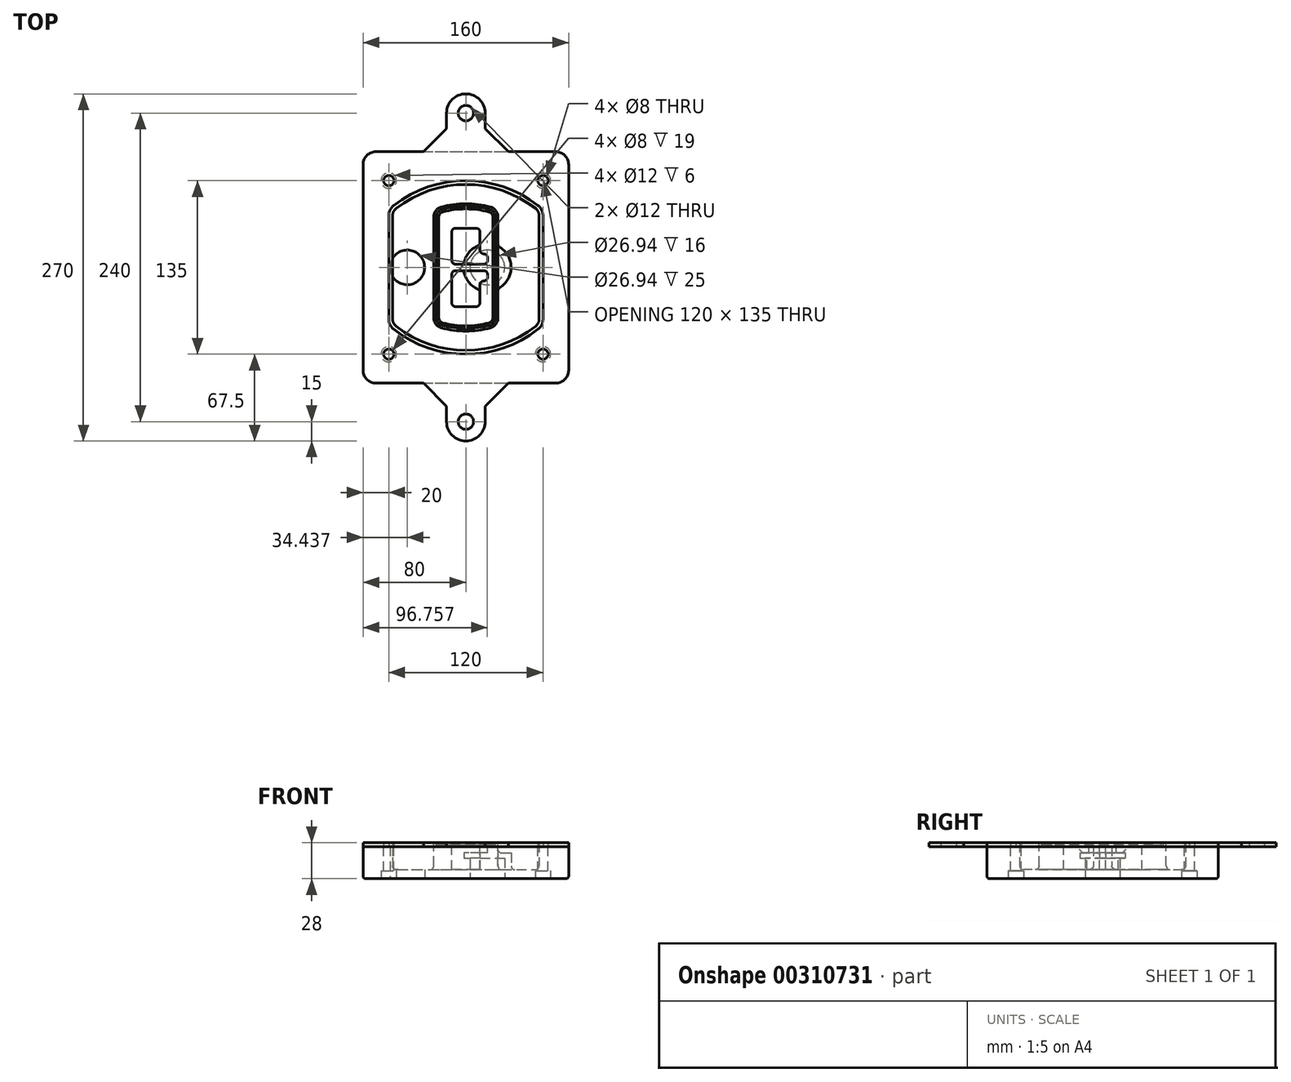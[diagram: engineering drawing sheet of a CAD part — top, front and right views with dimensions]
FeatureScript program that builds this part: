
annotation { "Feature Type Name" : "Feature", "Feature Type Description" : "" }
export const myFeature = defineFeature(function(context is Context, id is Id, definition is map)
    precondition{}
    {
        {
            var Q0;
            Q0=qCreatedBy(makeId("Top.planeOp"),FACE);
            var sketch = newSketch(context, id + "F0", { "sketchPlane" : qUnion([Q0])});
            skPoint(sketch, "E0.rect.middle", {"position": v(0, 0) * mm});
            skLineSegment(sketch, "E1.bottom", {"start": v(-70, -90) * mm, "end": v(70, -90) * mm});
            skLineSegment(sketch, "E1.top", {"start": v(-70, 90) * mm, "end": v(70, 90) * mm});
            skLineSegment(sketch, "E1.left", {"start": v(-80, -80) * mm, "end": v(-80, 80) * mm});
            skLineSegment(sketch, "E1.right", {"start": v(80, -80) * mm, "end": v(80, 80) * mm});
            skLineSegment(sketch, "E2", {"start": v(-80, 90) * mm, "end": v(80, -90) * mm, "construction": true});
            skLineSegment(sketch, "E3", {"start": v(80, 90) * mm, "end": v(-80, -90) * mm, "construction": true});
            skCircle(sketch, "E4", {"center": v(-60, 67.5) * mm, "radius": 4 * mm});
            skCircle(sketch, "E5", {"center": v(60, 67.5) * mm, "radius": 4 * mm});
            skCircle(sketch, "E6", {"center": v(60, -67.5) * mm, "radius": 4 * mm});
            skCircle(sketch, "E7", {"center": v(-60, -67.5) * mm, "radius": 4 * mm});
            skLineSegment(sketch, "E8", {"start": v(-60, 67.5) * mm, "end": v(60, 67.5) * mm, "construction": true});
            skLineSegment(sketch, "E9", {"start": v(60, 67.5) * mm, "end": v(60, -67.5) * mm, "construction": true});
            skLineSegment(sketch, "E10", {"start": v(60, -67.5) * mm, "end": v(-60, -67.5) * mm, "construction": true});
            skLineSegment(sketch, "E11", {"start": v(-60, -67.5) * mm, "end": v(-60, 67.5) * mm, "construction": true});
            skLineSegment(sketch, "E12", {"start": v(-60, 40.3) * mm, "end": v(-60, -40.3) * mm});
            skLineSegment(sketch, "E13", {"start": v(60, 40.3) * mm, "end": v(60, -40.3) * mm});
            skArc(sketch, "E14", {"start": v(56.15, 48.18) * mm, "mid": v(0, 67.5) * mm, "end": v(-56.15, 48.18) * mm});
            skArc(sketch, "E15", {"start": v(-56.15, -48.18) * mm, "mid": v(0, -67.5) * mm, "end": v(56.15, -48.18) * mm});
            skLineSegment(sketch, "E16", {"start": v(-60, 0) * mm, "end": v(60, 0) * mm, "construction": true});
            skPoint(sketch, "E17.visualSharp", {"position": v(-60, -45) * mm});
            skArc(sketch, "E17.filletArc", {"start": v(-60, -40.3) * mm, "mid": v(-58.99, -44.68) * mm, "end": v(-56.15, -48.18) * mm});
            skPoint(sketch, "E18.visualSharp", {"position": v(-60, 45) * mm});
            skArc(sketch, "E18.filletArc", {"start": v(-56.15, 48.18) * mm, "mid": v(-58.99, 44.68) * mm, "end": v(-60, 40.3) * mm});
            skPoint(sketch, "E19.visualSharp", {"position": v(60, 45) * mm});
            skArc(sketch, "E19.filletArc", {"start": v(60, 40.3) * mm, "mid": v(58.99, 44.68) * mm, "end": v(56.15, 48.18) * mm});
            skPoint(sketch, "E20.visualSharp", {"position": v(60, -45) * mm});
            skArc(sketch, "E20.filletArc", {"start": v(56.15, -48.18) * mm, "mid": v(58.99, -44.68) * mm, "end": v(60, -40.3) * mm});
            skPoint(sketch, "E21.visualSharp", {"position": v(-80, 90) * mm});
            skArc(sketch, "E21.filletArc", {"start": v(-70, 90) * mm, "mid": v(-77.07, 87.07) * mm, "end": v(-80, 80) * mm});
            skPoint(sketch, "E22.visualSharp", {"position": v(80, 90) * mm});
            skArc(sketch, "E22.filletArc", {"start": v(80, 80) * mm, "mid": v(77.07, 87.07) * mm, "end": v(70, 90) * mm});
            skPoint(sketch, "E23.visualSharp", {"position": v(80, -90) * mm});
            skArc(sketch, "E23.filletArc", {"start": v(70, -90) * mm, "mid": v(77.07, -87.07) * mm, "end": v(80, -80) * mm});
            skPoint(sketch, "E24.visualSharp", {"position": v(-80, -90) * mm});
            skArc(sketch, "E24.filletArc", {"start": v(-80, -80) * mm, "mid": v(-77.07, -87.07) * mm, "end": v(-70, -90) * mm});
            skArc(sketch, "E25.0", {"start": v(57, 40.3) * mm, "mid": v(56.3, 43.36) * mm, "end": v(54.3, 45.81) * mm});
            skLineSegment(sketch, "E25.1", {"start": v(57, 40.3) * mm, "end": v(57, -40.3) * mm});
            skArc(sketch, "E25.2", {"start": v(54.3, -45.81) * mm, "mid": v(56.3, -43.36) * mm, "end": v(57, -40.3) * mm});
            skArc(sketch, "E25.3", {"start": v(-54.3, -45.81) * mm, "mid": v(0, -64.5) * mm, "end": v(54.3, -45.81) * mm});
            skArc(sketch, "E25.4", {"start": v(-57, -40.3) * mm, "mid": v(-56.3, -43.36) * mm, "end": v(-54.3, -45.81) * mm});
            skArc(sketch, "E25.5", {"start": v(54.3, 45.81) * mm, "mid": v(0, 64.5) * mm, "end": v(-54.3, 45.81) * mm});
            skLineSegment(sketch, "E25.6", {"start": v(-57, 40.3) * mm, "end": v(-57, -40.3) * mm});
            skArc(sketch, "E25.7", {"start": v(-54.3, 45.81) * mm, "mid": v(-56.3, 43.36) * mm, "end": v(-57, 40.3) * mm});
            skArc(sketch, "E26.0", {"start": v(-58.62, 51.33) * mm, "mid": v(-62.58, 46.43) * mm, "end": v(-64, 40.3) * mm});
            skArc(sketch, "E26.1", {"start": v(58.62, 51.33) * mm, "mid": v(0, 71.5) * mm, "end": v(-58.62, 51.33) * mm});
            skArc(sketch, "E26.2", {"start": v(64, 40.3) * mm, "mid": v(62.58, 46.43) * mm, "end": v(58.62, 51.33) * mm});
            skLineSegment(sketch, "E26.3", {"start": v(64, 40.3) * mm, "end": v(64, -40.3) * mm});
            skArc(sketch, "E26.4", {"start": v(58.62, -51.33) * mm, "mid": v(62.58, -46.43) * mm, "end": v(64, -40.3) * mm});
            skLineSegment(sketch, "E26.5", {"start": v(-64, 40.3) * mm, "end": v(-64, -40.3) * mm});
            skArc(sketch, "E26.6", {"start": v(-58.62, -51.33) * mm, "mid": v(0, -71.5) * mm, "end": v(58.62, -51.33) * mm});
            skArc(sketch, "E26.7", {"start": v(-64, -40.3) * mm, "mid": v(-62.58, -46.43) * mm, "end": v(-58.62, -51.33) * mm});
            skSolve(sketch);
        }
        {
            var Q0;
            Q0=makeQuery(id+"F0.imprint","IMPRINT",FACE,{"disambiguationData":[TD([[makeQuery(id+"F0.imprint","IMPRINT",EDGE,{"derivedFrom":sQuery(id+"F0.wireOp",EDGE,"E1.bottom")}),1.0]])]});
            var Q1;
            Q1=makeQuery(id+"F0.imprint","IMPRINT",FACE,{"disambiguationData":[TD([[makeQuery(id+"F0.imprint","IMPRINT",EDGE,{"derivedFrom":sQuery(id+"F0.wireOp",EDGE,"E12")}),1.0]])]});
            var Q2;
            Q2=makeQuery(id+"F0.imprint","IMPRINT",FACE,{"disambiguationData":[TD([[makeQuery(id+"F0.imprint","IMPRINT",EDGE,{"derivedFrom":sQuery(id+"F0.wireOp",EDGE,"E25.0")}),1.0]])]});
            var Q3;
            Q3=makeQuery(id+"F0.imprint","IMPRINT",FACE,{"disambiguationData":[TD([[makeQuery(id+"F0.imprint","IMPRINT",EDGE,{"derivedFrom":sQuery(id+"F0.wireOp",EDGE,"E12")}),-1.0]])]});
            extrude(context, id + "F1", {"entities" : qUnion([Q0, Q1, Q2, Q3]), "oppositeDirection" : true, "depth" : 25 * mm});
        }
        {
            var Q0;
            Q0=makeQuery(id+"F0.imprint","IMPRINT",FACE,{"disambiguationData":[TD([[makeQuery(id+"F0.imprint","IMPRINT",EDGE,{"derivedFrom":sQuery(id+"F0.wireOp",EDGE,"E12")}),1.0]])]});
            extrude(context, id + "F2", {"entities" : qUnion([Q0]), "operationType" : NewBodyOperationType.ADD, "depth" : 3 * mm});
        }
        {
            var Q0;
            Q0=makeQuery(id+"F0.imprint","IMPRINT",FACE,{"disambiguationData":[TD([[makeQuery(id+"F0.imprint","IMPRINT",EDGE,{"derivedFrom":sQuery(id+"F0.wireOp",EDGE,"E25.0")}),1.0]])]});
            extrude(context, id + "F3", {"entities" : qUnion([Q0]), "operationType" : NewBodyOperationType.REMOVE, "oppositeDirection" : true, "depth" : 18 * mm});
        }
        {
            var Q0;
            Q0=makeQuery(id+"F2.opExtrude","CAP_FACE",FACE,{"disambiguationData":[OSD([sQuery(id+"F0.wireOp",EDGE,"E12"),sQuery(id+"F0.wireOp",EDGE,"E13"),sQuery(id+"F0.wireOp",EDGE,"E14"),sQuery(id+"F0.wireOp",EDGE,"E15"),sQuery(id+"F0.wireOp",EDGE,"E17.filletArc"),sQuery(id+"F0.wireOp",EDGE,"E18.filletArc"),sQuery(id+"F0.wireOp",EDGE,"E19.filletArc"),sQuery(id+"F0.wireOp",EDGE,"E20.filletArc"),sQuery(id+"F0.wireOp",EDGE,"E25.0"),sQuery(id+"F0.wireOp",EDGE,"E25.1"),sQuery(id+"F0.wireOp",EDGE,"E25.2"),sQuery(id+"F0.wireOp",EDGE,"E25.3"),sQuery(id+"F0.wireOp",EDGE,"E25.4"),sQuery(id+"F0.wireOp",EDGE,"E25.5"),sQuery(id+"F0.wireOp",EDGE,"E25.6"),sQuery(id+"F0.wireOp",EDGE,"E25.7")])],"isStart":false});
            var sketch = newSketch(context, id + "F4", { "sketchPlane" : qUnion([Q0])});
            skArc(sketch, "E27.0", {"start": v(-19.08, -46.97) * mm, "mid": v(0, -49.5) * mm, "end": v(19.08, -46.97) * mm});
            skArc(sketch, "E28.0", {"start": v(19.08, 46.97) * mm, "mid": v(0, 49.5) * mm, "end": v(-19.08, 46.97) * mm});
            skLineSegment(sketch, "E29", {"start": v(-25, 39.25) * mm, "end": v(-25, -39.25) * mm});
            skLineSegment(sketch, "E30", {"start": v(25, 39.25) * mm, "end": v(25, -39.25) * mm});
            skLineSegment(sketch, "E31", {"start": v(-25, 45.1) * mm, "end": v(25, 45.1) * mm, "construction": true});
            skLineSegment(sketch, "E32", {"start": v(-25, -45.1) * mm, "end": v(25, -45.1) * mm, "construction": true});
            skPoint(sketch, "E33.visualSharp", {"position": v(-25, 45.1) * mm});
            skArc(sketch, "E33.filletArc", {"start": v(-19.08, 46.97) * mm, "mid": v(-23.35, 44.11) * mm, "end": v(-25, 39.25) * mm});
            skPoint(sketch, "E34.visualSharp", {"position": v(25, 45.1) * mm});
            skArc(sketch, "E34.filletArc", {"start": v(25, 39.25) * mm, "mid": v(23.35, 44.11) * mm, "end": v(19.08, 46.97) * mm});
            skPoint(sketch, "E35.visualSharp", {"position": v(25, -45.1) * mm});
            skArc(sketch, "E35.filletArc", {"start": v(19.08, -46.97) * mm, "mid": v(23.35, -44.11) * mm, "end": v(25, -39.25) * mm});
            skPoint(sketch, "E36.visualSharp", {"position": v(-25, -45.1) * mm});
            skArc(sketch, "E36.filletArc", {"start": v(-25, -39.25) * mm, "mid": v(-23.35, -44.11) * mm, "end": v(-19.08, -46.97) * mm});
            skArc(sketch, "E37.0", {"start": v(54.3, 45.81) * mm, "mid": v(0, 64.5) * mm, "end": v(-54.3, 45.81) * mm});
            skArc(sketch, "E37.1", {"start": v(-54.3, 45.81) * mm, "mid": v(-56.3, 43.36) * mm, "end": v(-57, 40.3) * mm});
            skLineSegment(sketch, "E37.2", {"start": v(-57, 40.3) * mm, "end": v(-57, -40.3) * mm});
            skArc(sketch, "E37.3", {"start": v(-57, -40.3) * mm, "mid": v(-56.3, -43.36) * mm, "end": v(-54.3, -45.81) * mm});
            skArc(sketch, "E37.4", {"start": v(-54.3, -45.81) * mm, "mid": v(0, -64.5) * mm, "end": v(54.3, -45.81) * mm});
            skArc(sketch, "E37.5", {"start": v(54.3, -45.81) * mm, "mid": v(56.3, -43.36) * mm, "end": v(57, -40.3) * mm});
            skLineSegment(sketch, "E37.6", {"start": v(57, 40.3) * mm, "end": v(57, -40.3) * mm});
            skArc(sketch, "E37.7", {"start": v(57, 40.3) * mm, "mid": v(56.3, 43.36) * mm, "end": v(54.3, 45.81) * mm});
            skLineSegment(sketch, "E38.0", {"start": v(23, 39.25) * mm, "end": v(23, -39.25) * mm});
            skArc(sketch, "E38.1", {"start": v(18.56, -45.04) * mm, "mid": v(21.76, -42.9) * mm, "end": v(23, -39.25) * mm});
            skArc(sketch, "E38.2", {"start": v(-18.56, -45.04) * mm, "mid": v(0, -47.5) * mm, "end": v(18.56, -45.04) * mm});
            skArc(sketch, "E38.3", {"start": v(-23, -39.25) * mm, "mid": v(-21.76, -42.9) * mm, "end": v(-18.56, -45.04) * mm});
            skLineSegment(sketch, "E38.4", {"start": v(-23, 39.25) * mm, "end": v(-23, -39.25) * mm});
            skArc(sketch, "E38.5", {"start": v(23, 39.25) * mm, "mid": v(21.76, 42.9) * mm, "end": v(18.56, 45.04) * mm});
            skArc(sketch, "E38.6", {"start": v(-18.56, 45.04) * mm, "mid": v(-21.76, 42.9) * mm, "end": v(-23, 39.25) * mm});
            skArc(sketch, "E38.7", {"start": v(18.56, 45.04) * mm, "mid": v(0, 47.5) * mm, "end": v(-18.56, 45.04) * mm});
            skArc(sketch, "E39.0", {"start": v(21, 39.25) * mm, "mid": v(20.18, 41.68) * mm, "end": v(18.04, 43.1) * mm});
            skLineSegment(sketch, "E39.1", {"start": v(21, 39.25) * mm, "end": v(21, -39.25) * mm});
            skArc(sketch, "E39.2", {"start": v(18.04, -43.1) * mm, "mid": v(20.18, -41.68) * mm, "end": v(21, -39.25) * mm});
            skArc(sketch, "E39.3", {"start": v(-18.04, -43.1) * mm, "mid": v(0, -45.5) * mm, "end": v(18.04, -43.1) * mm});
            skArc(sketch, "E39.4", {"start": v(-21, -39.25) * mm, "mid": v(-20.18, -41.68) * mm, "end": v(-18.04, -43.1) * mm});
            skArc(sketch, "E39.5", {"start": v(18.04, 43.1) * mm, "mid": v(0, 45.5) * mm, "end": v(-18.04, 43.1) * mm});
            skLineSegment(sketch, "E39.6", {"start": v(-21, 39.25) * mm, "end": v(-21, -39.25) * mm});
            skArc(sketch, "E39.7", {"start": v(-18.04, 43.1) * mm, "mid": v(-20.18, 41.68) * mm, "end": v(-21, 39.25) * mm});
            skLineSegment(sketch, "E40", {"start": v(-25, 0) * mm, "end": v(25, 0) * mm, "construction": true});
            skLineSegment(sketch, "E41", {"start": v(-11, 5.5) * mm, "end": v(-11, 27.5) * mm});
            skLineSegment(sketch, "E42", {"start": v(-8, 30.5) * mm, "end": v(8, 30.5) * mm});
            skLineSegment(sketch, "E43", {"start": v(11, 27.5) * mm, "end": v(11, 13.5) * mm});
            skLineSegment(sketch, "E44", {"start": v(14, 10.5) * mm, "end": v(14, 10.5) * mm});
            skLineSegment(sketch, "E45", {"start": v(17, 7.5) * mm, "end": v(17, 5.5) * mm});
            skLineSegment(sketch, "E46", {"start": v(14, 2.5) * mm, "end": v(-8, 2.5) * mm});
            skPoint(sketch, "E47.visualSharp", {"position": v(-11, 30.5) * mm});
            skArc(sketch, "E47.filletArc", {"start": v(-8, 30.5) * mm, "mid": v(-10.12, 29.62) * mm, "end": v(-11, 27.5) * mm});
            skPoint(sketch, "E48.visualSharp", {"position": v(11, 30.5) * mm});
            skArc(sketch, "E48.filletArc", {"start": v(11, 27.5) * mm, "mid": v(10.12, 29.62) * mm, "end": v(8, 30.5) * mm});
            skPoint(sketch, "E49.visualSharp", {"position": v(11, 10.5) * mm});
            skArc(sketch, "E49.filletArc", {"start": v(11, 13.5) * mm, "mid": v(11.88, 11.38) * mm, "end": v(14, 10.5) * mm});
            skPoint(sketch, "E50.visualSharp", {"position": v(17, 10.5) * mm});
            skArc(sketch, "E50.filletArc", {"start": v(17, 7.5) * mm, "mid": v(16.12, 9.62) * mm, "end": v(14, 10.5) * mm});
            skPoint(sketch, "E51.visualSharp", {"position": v(17, 2.5) * mm});
            skArc(sketch, "E51.filletArc", {"start": v(14, 2.5) * mm, "mid": v(16.12, 3.38) * mm, "end": v(17, 5.5) * mm});
            skPoint(sketch, "E52.visualSharp", {"position": v(-11, 2.5) * mm});
            skArc(sketch, "E52.filletArc", {"start": v(-11, 5.5) * mm, "mid": v(-10.12, 3.38) * mm, "end": v(-8, 2.5) * mm});
            skLineSegment(sketch, "E53.0.MirrorCS", {"start": v(14, -2.5) * mm, "end": v(-8, -2.5) * mm});
            skArc(sketch, "E54.0.MirrorCS", {"start": v(-11, -5.5) * mm, "mid": v(-10.12, -3.38) * mm, "end": v(-8, -2.5) * mm});
            skLineSegment(sketch, "E55.0.MirrorCS", {"start": v(-11, -5.5) * mm, "end": v(-11, -27.5) * mm});
            skArc(sketch, "E56.0.MirrorCS", {"start": v(-8, -30.5) * mm, "mid": v(-10.12, -29.62) * mm, "end": v(-11, -27.5) * mm});
            skLineSegment(sketch, "E57.0.MirrorCS", {"start": v(-8, -30.5) * mm, "end": v(8, -30.5) * mm});
            skArc(sketch, "E58.0.MirrorCS", {"start": v(11, -27.5) * mm, "mid": v(10.12, -29.62) * mm, "end": v(8, -30.5) * mm});
            skLineSegment(sketch, "E59.0.MirrorCS", {"start": v(11, -27.5) * mm, "end": v(11, -13.5) * mm});
            skArc(sketch, "E60.0.MirrorCS", {"start": v(11, -13.5) * mm, "mid": v(11.88, -11.38) * mm, "end": v(14, -10.5) * mm});
            skArc(sketch, "E61.0.MirrorCS", {"start": v(17, -7.5) * mm, "mid": v(16.12, -9.62) * mm, "end": v(14, -10.5) * mm});
            skLineSegment(sketch, "E62.0.MirrorCS", {"start": v(17, -7.5) * mm, "end": v(17, -5.5) * mm});
            skArc(sketch, "E63.0.MirrorCS", {"start": v(14, -2.5) * mm, "mid": v(16.12, -3.38) * mm, "end": v(17, -5.5) * mm});
            skSolve(sketch);
        }
        {
            var Q0;
            Q0=makeQuery(id+"F4.imprint","IMPRINT",FACE,{"disambiguationData":[TD([[makeQuery(id+"F4.imprint","IMPRINT",EDGE,{"derivedFrom":sQuery(id+"F4.wireOp",EDGE,"E27.0")}),1.0]])]});
            var Q1;
            Q1=makeQuery(id+"F4.imprint","IMPRINT",FACE,{"disambiguationData":[TD([[makeQuery(id+"F4.imprint","IMPRINT",EDGE,{"derivedFrom":sQuery(id+"F4.wireOp",EDGE,"E38.0")}),-1.0]])]});
            var Q2;
            Q2=makeQuery(id+"F4.imprint","IMPRINT",FACE,{"disambiguationData":[TD([[makeQuery(id+"F4.imprint","IMPRINT",EDGE,{"derivedFrom":sQuery(id+"F4.wireOp",EDGE,"E39.0")}),1.0]])]});
            extrude(context, id + "F5", {"entities" : qUnion([Q0, Q1, Q2]), "operationType" : NewBodyOperationType.ADD, "endBound" : BoundingType.UP_TO_NEXT, "oppositeDirection" : true, "depth" : 25 * mm});
        }
        {
            var Q0;
            Q0=makeQuery(id+"F4.imprint","IMPRINT",FACE,{"disambiguationData":[TD([[makeQuery(id+"F4.imprint","IMPRINT",EDGE,{"derivedFrom":sQuery(id+"F4.wireOp",EDGE,"E38.0")}),-1.0]])]});
            extrude(context, id + "F6", {"entities" : qUnion([Q0]), "operationType" : NewBodyOperationType.REMOVE, "oppositeDirection" : true, "depth" : 2 * mm});
        }
        {
            var Q0;
            Q0=makeQuery(id+"F1.opExtrude","CAP_FACE",FACE,{"disambiguationData":[OSD([sQuery(id+"F0.wireOp",EDGE,"E1.bottom"),sQuery(id+"F0.wireOp",EDGE,"E1.top"),sQuery(id+"F0.wireOp",EDGE,"E1.left"),sQuery(id+"F0.wireOp",EDGE,"E1.right"),sQuery(id+"F0.wireOp",EDGE,"E4"),sQuery(id+"F0.wireOp",EDGE,"E5"),sQuery(id+"F0.wireOp",EDGE,"E6"),sQuery(id+"F0.wireOp",EDGE,"E7"),sQuery(id+"F0.wireOp",EDGE,"E21.filletArc"),sQuery(id+"F0.wireOp",EDGE,"E22.filletArc"),sQuery(id+"F0.wireOp",EDGE,"E23.filletArc"),sQuery(id+"F0.wireOp",EDGE,"E24.filletArc")])],"isStart":false});
            var sketch = newSketch(context, id + "F7", { "sketchPlane" : qUnion([Q0])});
            skCircle(sketch, "E64", {"center": v(16.76, 0) * mm, "radius": 13.47 * mm});
            skCircle(sketch, "E65", {"center": v(-45.56, 0) * mm, "radius": 13.47 * mm});
            skLineSegment(sketch, "E66", {"start": v(80, 0) * mm, "end": v(-80, 0) * mm});
            skCircle(sketch, "E67", {"center": v(16.76, 0) * mm, "radius": 18.47 * mm});
            skCircle(sketch, "E68", {"center": v(60, -67.5) * mm, "radius": 6 * mm});
            skCircle(sketch, "E69", {"center": v(-60, -67.5) * mm, "radius": 6 * mm});
            skCircle(sketch, "E70", {"center": v(-60, 67.5) * mm, "radius": 6 * mm});
            skCircle(sketch, "E71", {"center": v(60, 67.5) * mm, "radius": 6 * mm});
            skSolve(sketch);
        }
        {
            var Q0;
            {var subQ1=sQuery(id+"F7.wireOp",EDGE,"E66");var subQ4=sQuery(id+"F7.wireOp",EDGE,"E64");var subQ6=makeQuery(id+"F7.imprint","INTERSECT",VERTEX,{"disambiguationData":[OD(0.0)],"derivedFrom":[subQ4,subQ1]});Q0=makeQuery(id+"F7.imprint","IMPRINT",FACE,{"disambiguationData":[TD([[makeQuery(id+"F7.imprint","IMPRINT",EDGE,{"disambiguationData":[TD([[subQ6,-1.0]])],"derivedFrom":subQ4}),-1.0]])]});}
            var Q1;
            {var subQ0=sQuery(id+"F7.wireOp",EDGE,"E66");var subQ1=sQuery(id+"F7.wireOp",EDGE,"E64");var subQ3=makeQuery(id+"F7.imprint","INTERSECT",VERTEX,{"disambiguationData":[OD(0.0)],"derivedFrom":[subQ1,subQ0]});Q1=makeQuery(id+"F7.imprint","IMPRINT",FACE,{"disambiguationData":[TD([[makeQuery(id+"F7.imprint","IMPRINT",EDGE,{"disambiguationData":[TD([[subQ3,-1.0]])],"derivedFrom":subQ1}),1.0]])]});}
            var Q2;
            {var subQ0=sQuery(id+"F7.wireOp",EDGE,"E66");var subQ1=sQuery(id+"F7.wireOp",EDGE,"E64");var subQ3=makeQuery(id+"F7.imprint","INTERSECT",VERTEX,{"disambiguationData":[OD(0.0)],"derivedFrom":[subQ1,subQ0]});Q2=makeQuery(id+"F7.imprint","IMPRINT",FACE,{"disambiguationData":[TD([[makeQuery(id+"F7.imprint","IMPRINT",EDGE,{"disambiguationData":[TD([[subQ3,1.0]])],"derivedFrom":subQ1}),1.0]])]});}
            var Q3;
            {var subQ1=sQuery(id+"F7.wireOp",EDGE,"E66");var subQ4=sQuery(id+"F7.wireOp",EDGE,"E64");var subQ6=makeQuery(id+"F7.imprint","INTERSECT",VERTEX,{"disambiguationData":[OD(0.0)],"derivedFrom":[subQ4,subQ1]});Q3=makeQuery(id+"F7.imprint","IMPRINT",FACE,{"disambiguationData":[TD([[makeQuery(id+"F7.imprint","IMPRINT",EDGE,{"disambiguationData":[TD([[subQ6,1.0]])],"derivedFrom":subQ4}),-1.0]])]});}
            extrude(context, id + "F8", {"entities" : qUnion([Q0, Q1, Q2, Q3]), "operationType" : NewBodyOperationType.ADD, "oppositeDirection" : true, "depth" : 20 * mm});
        }
        {
            var Q0;
            {var subQ0=sQuery(id+"F7.wireOp",EDGE,"E66");var subQ1=sQuery(id+"F7.wireOp",EDGE,"E64");var subQ3=makeQuery(id+"F7.imprint","INTERSECT",VERTEX,{"disambiguationData":[OD(0.0)],"derivedFrom":[subQ1,subQ0]});Q0=makeQuery(id+"F7.imprint","IMPRINT",FACE,{"disambiguationData":[TD([[makeQuery(id+"F7.imprint","IMPRINT",EDGE,{"disambiguationData":[TD([[subQ3,-1.0]])],"derivedFrom":subQ1}),1.0]])]});}
            var Q1;
            {var subQ0=sQuery(id+"F7.wireOp",EDGE,"E66");var subQ1=sQuery(id+"F7.wireOp",EDGE,"E64");var subQ3=makeQuery(id+"F7.imprint","INTERSECT",VERTEX,{"disambiguationData":[OD(0.0)],"derivedFrom":[subQ1,subQ0]});Q1=makeQuery(id+"F7.imprint","IMPRINT",FACE,{"disambiguationData":[TD([[makeQuery(id+"F7.imprint","IMPRINT",EDGE,{"disambiguationData":[TD([[subQ3,1.0]])],"derivedFrom":subQ1}),1.0]])]});}
            extrude(context, id + "F9", {"entities" : qUnion([Q0, Q1]), "operationType" : NewBodyOperationType.REMOVE, "oppositeDirection" : true, "depth" : 16 * mm});
        }
        {
            var Q0;
            {var subQ0=sQuery(id+"F7.wireOp",EDGE,"E66");var subQ1=sQuery(id+"F7.wireOp",EDGE,"E65");var subQ3=makeQuery(id+"F7.imprint","INTERSECT",VERTEX,{"disambiguationData":[OD(0.0)],"derivedFrom":[subQ1,subQ0]});Q0=makeQuery(id+"F7.imprint","IMPRINT",FACE,{"disambiguationData":[TD([[makeQuery(id+"F7.imprint","IMPRINT",EDGE,{"disambiguationData":[TD([[subQ3,-1.0]])],"derivedFrom":subQ1}),1.0]])]});}
            var Q1;
            {var subQ0=sQuery(id+"F7.wireOp",EDGE,"E66");var subQ1=sQuery(id+"F7.wireOp",EDGE,"E65");var subQ3=makeQuery(id+"F7.imprint","INTERSECT",VERTEX,{"disambiguationData":[OD(0.0)],"derivedFrom":[subQ1,subQ0]});Q1=makeQuery(id+"F7.imprint","IMPRINT",FACE,{"disambiguationData":[TD([[makeQuery(id+"F7.imprint","IMPRINT",EDGE,{"disambiguationData":[TD([[subQ3,1.0]])],"derivedFrom":subQ1}),1.0]])]});}
            extrude(context, id + "F10", {"entities" : qUnion([Q0, Q1]), "operationType" : NewBodyOperationType.REMOVE, "oppositeDirection" : true, "depth" : 25 * mm});
        }
        {
            var Q0;
            Q0=makeQuery(id+"F7.imprint","IMPRINT",FACE,{"disambiguationData":[TD([[makeQuery(id+"F7.imprint","IMPRINT",EDGE,{"derivedFrom":sQuery(id+"F7.wireOp",EDGE,"E68")}),1.0]])]});
            var Q1;
            Q1=makeQuery(id+"F7.imprint","IMPRINT",FACE,{"disambiguationData":[TD([[makeQuery(id+"F7.imprint","IMPRINT",EDGE,{"derivedFrom":makeQuery(id+"F1.opExtrude","CAP_EDGE",EDGE,{"disambiguationData":[OSD([sQuery(id+"F0.wireOp",EDGE,"E5")])],"isStart":false})}),-1.0]])]});
            var Q2;
            Q2=makeQuery(id+"F7.imprint","IMPRINT",FACE,{"disambiguationData":[TD([[makeQuery(id+"F7.imprint","IMPRINT",EDGE,{"derivedFrom":sQuery(id+"F7.wireOp",EDGE,"E69")}),1.0]])]});
            var Q3;
            Q3=makeQuery(id+"F7.imprint","IMPRINT",FACE,{"disambiguationData":[TD([[makeQuery(id+"F7.imprint","IMPRINT",EDGE,{"derivedFrom":makeQuery(id+"F1.opExtrude","CAP_EDGE",EDGE,{"disambiguationData":[OSD([sQuery(id+"F0.wireOp",EDGE,"E4")])],"isStart":false})}),-1.0]])]});
            var Q4;
            Q4=makeQuery(id+"F7.imprint","IMPRINT",FACE,{"disambiguationData":[TD([[makeQuery(id+"F7.imprint","IMPRINT",EDGE,{"derivedFrom":sQuery(id+"F7.wireOp",EDGE,"E70")}),1.0]])]});
            var Q5;
            Q5=makeQuery(id+"F7.imprint","IMPRINT",FACE,{"disambiguationData":[TD([[makeQuery(id+"F7.imprint","IMPRINT",EDGE,{"derivedFrom":makeQuery(id+"F1.opExtrude","CAP_EDGE",EDGE,{"disambiguationData":[OSD([sQuery(id+"F0.wireOp",EDGE,"E7")])],"isStart":false})}),-1.0]])]});
            var Q6;
            Q6=makeQuery(id+"F7.imprint","IMPRINT",FACE,{"disambiguationData":[TD([[makeQuery(id+"F7.imprint","IMPRINT",EDGE,{"derivedFrom":sQuery(id+"F7.wireOp",EDGE,"E71")}),1.0]])]});
            var Q7;
            Q7=makeQuery(id+"F7.imprint","IMPRINT",FACE,{"disambiguationData":[TD([[makeQuery(id+"F7.imprint","IMPRINT",EDGE,{"derivedFrom":makeQuery(id+"F1.opExtrude","CAP_EDGE",EDGE,{"disambiguationData":[OSD([sQuery(id+"F0.wireOp",EDGE,"E6")])],"isStart":false})}),-1.0]])]});
            extrude(context, id + "F11", {"entities" : qUnion([Q0, Q1, Q2, Q3, Q4, Q5, Q6, Q7]), "operationType" : NewBodyOperationType.REMOVE, "oppositeDirection" : true, "depth" : 6 * mm});
        }
        {
            var Q0;
            Q0=makeQuery(id+"F9.boolean.opBoolean","COPY",FACE,{"derivedFrom":makeQuery(id+"F9.opExtrude","CAP_FACE",FACE,{"disambiguationData":[OSD([sQuery(id+"F7.wireOp",EDGE,"E64")])],"isStart":false})});
            var sketch = newSketch(context, id + "F12", { "sketchPlane" : qUnion([Q0])});
            skArc(sketch, "E72.0", {"start": v(11, 17.55) * mm, "mid": v(2.57, 11.82) * mm, "end": v(-1.54, 2.5) * mm});
            skArc(sketch, "E72.1", {"start": v(-1.54, -2.5) * mm, "mid": v(2.57, -11.82) * mm, "end": v(11, -17.55) * mm});
            skLineSegment(sketch, "E73", {"start": v(-1.54, -2.5) * mm, "end": v(14, -2.5) * mm});
            skLineSegment(sketch, "E74.0", {"start": v(14, 2.5) * mm, "end": v(-1.54, 2.5) * mm});
            skArc(sketch, "E74.1", {"start": v(14, 2.5) * mm, "mid": v(16.12, 3.38) * mm, "end": v(17, 5.5) * mm});
            skLineSegment(sketch, "E74.2", {"start": v(17, 7.5) * mm, "end": v(17, 5.5) * mm});
            skArc(sketch, "E74.3", {"start": v(17, 7.5) * mm, "mid": v(16.12, 9.62) * mm, "end": v(14, 10.5) * mm});
            skArc(sketch, "E74.4", {"start": v(11, 13.5) * mm, "mid": v(11.88, 11.38) * mm, "end": v(14, 10.5) * mm});
            skLineSegment(sketch, "E74.5", {"start": v(11, 17.55) * mm, "end": v(11, 13.5) * mm});
            skLineSegment(sketch, "E74.7", {"start": v(14, -2.5) * mm, "end": v(-1.54, -2.5) * mm});
            skArc(sketch, "E74.8", {"start": v(14, -2.5) * mm, "mid": v(16.12, -3.38) * mm, "end": v(17, -5.5) * mm});
            skLineSegment(sketch, "E74.9", {"start": v(17, -7.5) * mm, "end": v(17, -5.5) * mm});
            skArc(sketch, "E74.10", {"start": v(17, -7.5) * mm, "mid": v(16.12, -9.62) * mm, "end": v(14, -10.5) * mm});
            skArc(sketch, "E74.11", {"start": v(11, -13.5) * mm, "mid": v(11.88, -11.38) * mm, "end": v(14, -10.5) * mm});
            skLineSegment(sketch, "E74.12", {"start": v(11, -17.55) * mm, "end": v(11, -13.5) * mm});
            skPoint(sketch, "E75.orphan", {"position": v(11, -27.5) * mm});
            skPoint(sketch, "E76.orphan", {"position": v(-8, -2.5) * mm});
            skPoint(sketch, "E77.orphan", {"position": v(-8, 2.5) * mm});
            skPoint(sketch, "E78.orphan", {"position": v(11, 27.5) * mm});
            skSolve(sketch);
        }
        {
            var Q0;
            {var subQ7=sQuery(id+"F12.wireOp",EDGE,"E72.0");var subQ14=sQuery(id+"F12.wireOp",EDGE,"E72.1");var subQ16=sQuery(id+"F12.wireOp",EDGE,"E74.1");var subQ18=sQuery(id+"F12.wireOp",EDGE,"E74.8");Q0=qUnion([makeQuery(id+"F12.imprint","IMPRINT",FACE,{"disambiguationData":[TD([[makeQuery(id+"F12.imprint","IMPRINT",EDGE,{"derivedFrom":subQ7}),1.0]])]}),makeQuery(id+"F12.imprint","IMPRINT",FACE,{"disambiguationData":[TD([[makeQuery(id+"F12.imprint","IMPRINT",EDGE,{"derivedFrom":subQ14}),1.0]])]}),makeQuery(id+"F12.imprint","IMPRINT",FACE,{"disambiguationData":[TD([[makeQuery(id+"F12.imprint","IMPRINT",EDGE,{"derivedFrom":subQ16}),1.0]])]}),makeQuery(id+"F12.imprint","IMPRINT",FACE,{"disambiguationData":[TD([[makeQuery(id+"F12.imprint","IMPRINT",EDGE,{"derivedFrom":subQ18}),-1.0]])]})]);}
            var Q1;
            Q1=makeQuery(id+"F5.boolean.opBoolean","SPLIT",FACE,{"disambiguationData":[TD([makeQuery(id+"F5.opExtrude","SWEPT_FACE",FACE,{"disambiguationData":[OSD([sQuery(id+"F4.wireOp",EDGE,"E41")])]})])],"derivedFrom":makeQuery(id+"F3.boolean.opBoolean","COPY",FACE,{"derivedFrom":makeQuery(id+"F3.opExtrude","CAP_FACE",FACE,{"disambiguationData":[OSD([sQuery(id+"F0.wireOp",EDGE,"E25.0"),sQuery(id+"F0.wireOp",EDGE,"E25.1"),sQuery(id+"F0.wireOp",EDGE,"E25.2"),sQuery(id+"F0.wireOp",EDGE,"E25.3"),sQuery(id+"F0.wireOp",EDGE,"E25.4"),sQuery(id+"F0.wireOp",EDGE,"E25.5"),sQuery(id+"F0.wireOp",EDGE,"E25.6"),sQuery(id+"F0.wireOp",EDGE,"E25.7")])],"isStart":false})})});
            extrude(context, id + "F13", {"entities" : qUnion([Q0]), "operationType" : NewBodyOperationType.REMOVE, "endBound" : BoundingType.UP_TO_SURFACE, "endBoundEntityFace" : qUnion([Q1]), "depth" : 25 * mm});
        }
        {
            var Q0;
            Q0=makeQuery(id+"F3.boolean.opBoolean","COPY",EDGE,{"derivedFrom":makeQuery(id+"F3.opExtrude","CAP_EDGE",EDGE,{"disambiguationData":[OSD([sQuery(id+"F0.wireOp",EDGE,"E25.6")])],"isStart":false})});
            var Q1;
            Q1=makeQuery(id+"F8.boolean.opBoolean","INTERSECT",EDGE,{"derivedFrom":[makeQuery(id+"F5.opExtrude","SWEPT_FACE",FACE,{"disambiguationData":[OSD([sQuery(id+"F4.wireOp",EDGE,"E30")])]}),makeQuery(id+"F8.opExtrude","CAP_FACE",FACE,{"disambiguationData":[OSD([sQuery(id+"F7.wireOp",EDGE,"E67")])],"isStart":false})]});
            var Q2;
            Q2=makeQuery(id+"F8.boolean.opBoolean","INTERSECT",EDGE,{"disambiguationData":[OD(1.0)],"derivedFrom":[makeQuery(id+"F5.opExtrude","SWEPT_FACE",FACE,{"disambiguationData":[OSD([sQuery(id+"F4.wireOp",EDGE,"E30")])]}),makeQuery(id+"F8.opExtrude","SWEPT_FACE",FACE,{"disambiguationData":[OSD([sQuery(id+"F7.wireOp",EDGE,"E67")])]})]});
            var Q3;
            {var subQ0=sQuery(id+"F4.wireOp",EDGE,"E30");Q3=makeQuery(id+"F8.boolean.opBoolean","SPLIT",EDGE,{"disambiguationData":[TD([makeQuery(id+"F5.opExtrude","SWEPT_FACE",FACE,{"disambiguationData":[OSD([sQuery(id+"F4.wireOp",EDGE,"E35.filletArc")])]})])],"derivedFrom":makeQuery(id+"F5.opExtrude","CAP_EDGE",EDGE,{"disambiguationData":[OSD([subQ0])],"isStart":false})});}
            var Q4;
            {var subQ0=sQuery(id+"F0.wireOp",EDGE,"E25.7");var subQ1=sQuery(id+"F0.wireOp",EDGE,"E25.1");var subQ2=sQuery(id+"F0.wireOp",EDGE,"E25.6");var subQ3=sQuery(id+"F0.wireOp",EDGE,"E25.5");var subQ4=sQuery(id+"F0.wireOp",EDGE,"E25.4");var subQ5=sQuery(id+"F0.wireOp",EDGE,"E25.0");var subQ6=sQuery(id+"F0.wireOp",EDGE,"E25.2");var subQ7=sQuery(id+"F0.wireOp",EDGE,"E25.3");Q4=makeQuery(id+"F8.boolean.opBoolean","INTERSECT",EDGE,{"derivedFrom":[makeQuery(id+"F5.boolean.opBoolean","SPLIT",FACE,{"disambiguationData":[TD([makeQuery(id+"F2.opExtrude","SWEPT_FACE",FACE,{"disambiguationData":[OSD([subQ5])]})])],"derivedFrom":makeQuery(id+"F3.boolean.opBoolean","COPY",FACE,{"derivedFrom":makeQuery(id+"F3.opExtrude","CAP_FACE",FACE,{"disambiguationData":[OSD([subQ5,subQ1,subQ6,subQ7,subQ4,subQ3,subQ2,subQ0])],"isStart":false})})}),makeQuery(id+"F8.opExtrude","SWEPT_FACE",FACE,{"disambiguationData":[OSD([sQuery(id+"F7.wireOp",EDGE,"E67")])]})]});}
            var Q5;
            Q5=makeQuery(id+"F8.boolean.opBoolean","INTERSECT",EDGE,{"disambiguationData":[OD(0.0)],"derivedFrom":[makeQuery(id+"F5.opExtrude","SWEPT_FACE",FACE,{"disambiguationData":[OSD([sQuery(id+"F4.wireOp",EDGE,"E30")])]}),makeQuery(id+"F8.opExtrude","SWEPT_FACE",FACE,{"disambiguationData":[OSD([sQuery(id+"F7.wireOp",EDGE,"E67")])]})]});
            fillet(context, id + "F14", {"entities" : qUnion([Q0, Q1, Q2, Q3, Q4, Q5]), "radius" : 3 * mm, "tangentPropagation" : true, "allowEdgeOverflow" : false});
        }
        {
            var Q0;
            Q0=makeQuery(id+"F1.opExtrude","CAP_EDGE",EDGE,{"disambiguationData":[OSD([sQuery(id+"F0.wireOp",EDGE,"E1.bottom")])],"isStart":false});
            fillet(context, id + "F15", {"entities" : qUnion([Q0]), "radius" : 2 * mm, "tangentPropagation" : true, "allowEdgeOverflow" : false});
        }
        {
            var Q0;
            {var subQ0=sQuery(id+"F0.wireOp",EDGE,"E21.filletArc");var subQ1=sQuery(id+"F0.wireOp",EDGE,"E7");var subQ2=sQuery(id+"F0.wireOp",EDGE,"E6");var subQ3=sQuery(id+"F0.wireOp",EDGE,"E5");var subQ4=sQuery(id+"F0.wireOp",EDGE,"E4");var subQ5=sQuery(id+"F0.wireOp",EDGE,"E22.filletArc");var subQ6=sQuery(id+"F0.wireOp",EDGE,"E1.bottom");var subQ7=sQuery(id+"F0.wireOp",EDGE,"E1.right");var subQ8=sQuery(id+"F0.wireOp",EDGE,"E1.top");var subQ9=sQuery(id+"F0.wireOp",EDGE,"E1.left");var subQ10=sQuery(id+"F0.wireOp",EDGE,"E23.filletArc");var subQ11=sQuery(id+"F0.wireOp",EDGE,"E24.filletArc");Q0=makeQuery(id+"F2.boolean.opBoolean","SPLIT",FACE,{"disambiguationData":[TD([makeQuery(id+"F1.opExtrude","SWEPT_FACE",FACE,{"disambiguationData":[OSD([subQ6])]})])],"derivedFrom":makeQuery(id+"F1.opExtrude","CAP_FACE",FACE,{"disambiguationData":[OSD([subQ6,subQ8,subQ9,subQ7,subQ4,subQ3,subQ2,subQ1,subQ0,subQ5,subQ10,subQ11])],"isStart":true})});}
            var sketch = newSketch(context, id + "F16", { "sketchPlane" : qUnion([Q0])});
            skLineSegment(sketch, "E79", {"start": v(0, 90) * mm, "end": v(0, 120) * mm, "construction": true});
            skCircle(sketch, "E80", {"center": v(0, 120) * mm, "radius": 6 * mm});
            skArc(sketch, "E81", {"start": v(15, 120) * mm, "mid": v(0, 135) * mm, "end": v(-15, 120) * mm});
            skLineSegment(sketch, "E82", {"start": v(-15, 120) * mm, "end": v(-15, 108) * mm});
            skLineSegment(sketch, "E83", {"start": v(15, 120) * mm, "end": v(15, 108) * mm});
            skLineSegment(sketch, "E84", {"start": v(-15, 108) * mm, "end": v(-33, 90) * mm});
            skLineSegment(sketch, "E85", {"start": v(15, 108) * mm, "end": v(33, 90) * mm});
            skLineSegment(sketch, "E86", {"start": v(-80, 0) * mm, "end": v(80, 0) * mm, "construction": true});
            skLineSegment(sketch, "E87.MirrorCS", {"start": v(15, -108) * mm, "end": v(33, -90) * mm});
            skLineSegment(sketch, "E88.MirrorCS", {"start": v(15, -120) * mm, "end": v(15, -108) * mm});
            skArc(sketch, "E89.MirrorCS", {"start": v(15, -120) * mm, "mid": v(0, -135) * mm, "end": v(-15, -120) * mm});
            skLineSegment(sketch, "E90.MirrorCS", {"start": v(-15, -120) * mm, "end": v(-15, -108) * mm});
            skLineSegment(sketch, "E91.MirrorCS", {"start": v(-15, -108) * mm, "end": v(-33, -90) * mm});
            skCircle(sketch, "E92.MirrorC", {"center": v(0, -120) * mm, "radius": 6 * mm});
            skSolve(sketch);
        }
        {
            var Q0;
            Q0=makeQuery(id+"F16.imprint","IMPRINT",FACE,{"disambiguationData":[TD([[makeQuery(id+"F16.imprint","IMPRINT",EDGE,{"derivedFrom":sQuery(id+"F16.wireOp",EDGE,"E80")}),-1.0]])]});
            var Q1;
            {var subQ0=sQuery(id+"F16.wireOp",EDGE,"E87.MirrorCS");Q1=makeQuery(id+"F16.imprint","IMPRINT",FACE,{"disambiguationData":[TD([[makeQuery(id+"F16.imprint","IMPRINT",EDGE,{"derivedFrom":subQ0}),1.0]])]});}
            var Q2;
            Q2=makeQuery(id+"F16.imprint","IMPRINT",FACE,{"disambiguationData":[TD([[makeQuery(id+"F16.imprint","IMPRINT",EDGE,{"derivedFrom":makeQuery(id+"F1.opExtrude","CAP_EDGE",EDGE,{"disambiguationData":[OSD([sQuery(id+"F0.wireOp",EDGE,"E1.left")])],"isStart":true})}),-1.0]])]});
            var Q3;
            Q3=makeQuery(id+"F2.opExtrude","CAP_FACE",FACE,{"disambiguationData":[OSD([sQuery(id+"F0.wireOp",EDGE,"E12"),sQuery(id+"F0.wireOp",EDGE,"E13"),sQuery(id+"F0.wireOp",EDGE,"E14"),sQuery(id+"F0.wireOp",EDGE,"E15"),sQuery(id+"F0.wireOp",EDGE,"E17.filletArc"),sQuery(id+"F0.wireOp",EDGE,"E18.filletArc"),sQuery(id+"F0.wireOp",EDGE,"E19.filletArc"),sQuery(id+"F0.wireOp",EDGE,"E20.filletArc"),sQuery(id+"F0.wireOp",EDGE,"E25.0"),sQuery(id+"F0.wireOp",EDGE,"E25.1"),sQuery(id+"F0.wireOp",EDGE,"E25.2"),sQuery(id+"F0.wireOp",EDGE,"E25.3"),sQuery(id+"F0.wireOp",EDGE,"E25.4"),sQuery(id+"F0.wireOp",EDGE,"E25.5"),sQuery(id+"F0.wireOp",EDGE,"E25.6"),sQuery(id+"F0.wireOp",EDGE,"E25.7")])],"isStart":false});
            var Q4;
            Q4=makeQuery(id+"F1.opExtrude","SWEPT_BODY",BODY,{"disambiguationData":[OSD([sQuery(id+"F0.wireOp",EDGE,"E1.bottom"),sQuery(id+"F0.wireOp",EDGE,"E1.top"),sQuery(id+"F0.wireOp",EDGE,"E1.left"),sQuery(id+"F0.wireOp",EDGE,"E1.right"),sQuery(id+"F0.wireOp",EDGE,"E4"),sQuery(id+"F0.wireOp",EDGE,"E5"),sQuery(id+"F0.wireOp",EDGE,"E6"),sQuery(id+"F0.wireOp",EDGE,"E7"),sQuery(id+"F0.wireOp",EDGE,"E21.filletArc"),sQuery(id+"F0.wireOp",EDGE,"E22.filletArc"),sQuery(id+"F0.wireOp",EDGE,"E23.filletArc"),sQuery(id+"F0.wireOp",EDGE,"E24.filletArc")])]});
            extrude(context, id + "F17", {"entities" : qUnion([Q0, Q1, Q2]), "endBound" : BoundingType.UP_TO_SURFACE, "endBoundEntityFace" : qUnion([Q3]), "endBoundEntityBody" : qUnion([Q4]), "depth" : 25 * mm});
        }
    });
